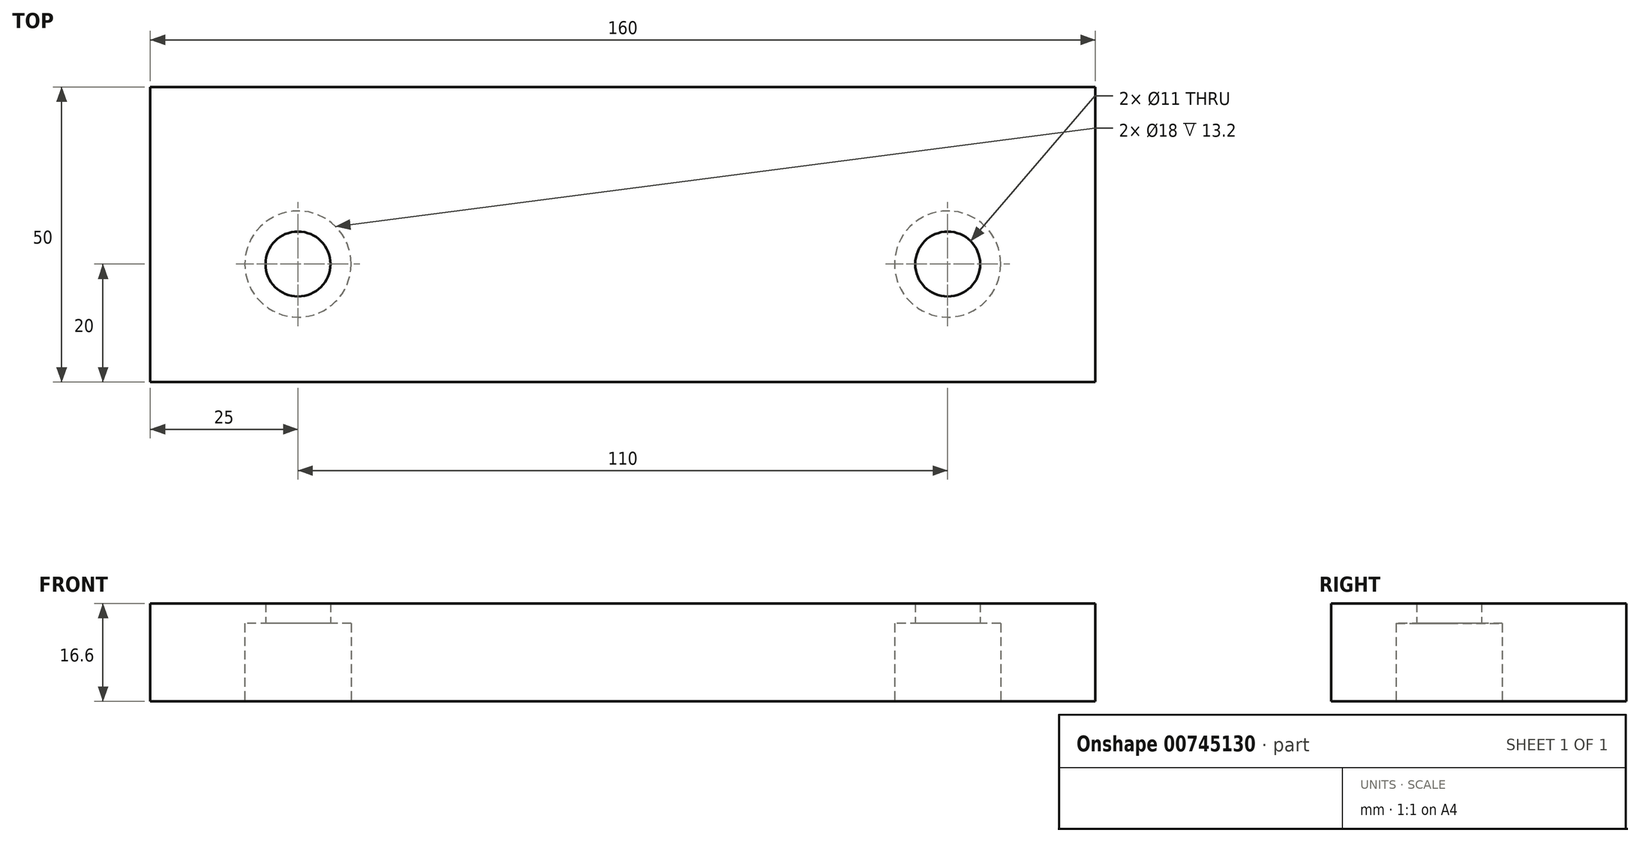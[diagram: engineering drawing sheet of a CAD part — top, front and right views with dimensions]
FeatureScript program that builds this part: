
annotation { "Feature Type Name" : "Feature", "Feature Type Description" : "" }
export const myFeature = defineFeature(function(context is Context, id is Id, definition is map)
    precondition{}
    {
        {
            var Q0;
            Q0=qCreatedBy(makeId("Top.planeOp"),FACE);
            var sketch = newSketch(context, id + "F0", { "sketchPlane" : qUnion([Q0])});
            skLineSegment(sketch, "E0.bottom", {"start": v(80, 25) * mm, "end": v(-80, 25) * mm});
            skLineSegment(sketch, "E0.top", {"start": v(80, -25) * mm, "end": v(-80, -25) * mm});
            skLineSegment(sketch, "E0.left", {"start": v(80, 25) * mm, "end": v(80, -25) * mm});
            skLineSegment(sketch, "E0.right", {"start": v(-80, 25) * mm, "end": v(-80, -25) * mm});
            skPoint(sketch, "E0.middle", {"position": v(0, 0) * mm});
            skCircle(sketch, "E1", {"center": v(-55, -5) * mm, "radius": 9 * mm});
            skCircle(sketch, "E2", {"center": v(55, -5) * mm, "radius": 9 * mm});
            skCircle(sketch, "E3", {"center": v(-55, -5) * mm, "radius": 5.5 * mm});
            skCircle(sketch, "E4", {"center": v(55, -5) * mm, "radius": 5.5 * mm});
            skSolve(sketch);
        }
        {
            var Q0;
            Q0=makeQuery(id+"F0.imprint","IMPRINT",FACE,{"disambiguationData":[TD([[makeQuery(id+"F0.imprint","IMPRINT",EDGE,{"derivedFrom":sQuery(id+"F0.wireOp",EDGE,"E0.bottom")}),1.0]])]});
            var Q1;
            Q1=makeQuery(id+"F0.imprint","IMPRINT",FACE,{"disambiguationData":[TD([[makeQuery(id+"F0.imprint","IMPRINT",EDGE,{"derivedFrom":sQuery(id+"F0.wireOp",EDGE,"E1")}),1.0]])]});
            var Q2;
            Q2=makeQuery(id+"F0.imprint","IMPRINT",FACE,{"disambiguationData":[TD([[makeQuery(id+"F0.imprint","IMPRINT",EDGE,{"derivedFrom":sQuery(id+"F0.wireOp",EDGE,"E2")}),1.0]])]});
            extrude(context, id + "F1", {"entities" : qUnion([Q0, Q1, Q2]), "depth" : 16.6 * mm, "offsetDistance" : 25 * mm});
        }
        {
            var Q0;
            Q0=makeQuery(id+"F0.imprint","IMPRINT",FACE,{"disambiguationData":[TD([[makeQuery(id+"F0.imprint","IMPRINT",EDGE,{"derivedFrom":sQuery(id+"F0.wireOp",EDGE,"E1")}),1.0]])]});
            var Q1;
            Q1=makeQuery(id+"F0.imprint","IMPRINT",FACE,{"disambiguationData":[TD([[makeQuery(id+"F0.imprint","IMPRINT",EDGE,{"derivedFrom":sQuery(id+"F0.wireOp",EDGE,"E2")}),1.0]])]});
            extrude(context, id + "F2", {"entities" : qUnion([Q0, Q1]), "operationType" : NewBodyOperationType.REMOVE, "depth" : 13.2 * mm, "offsetDistance" : 25 * mm});
        }
    });
